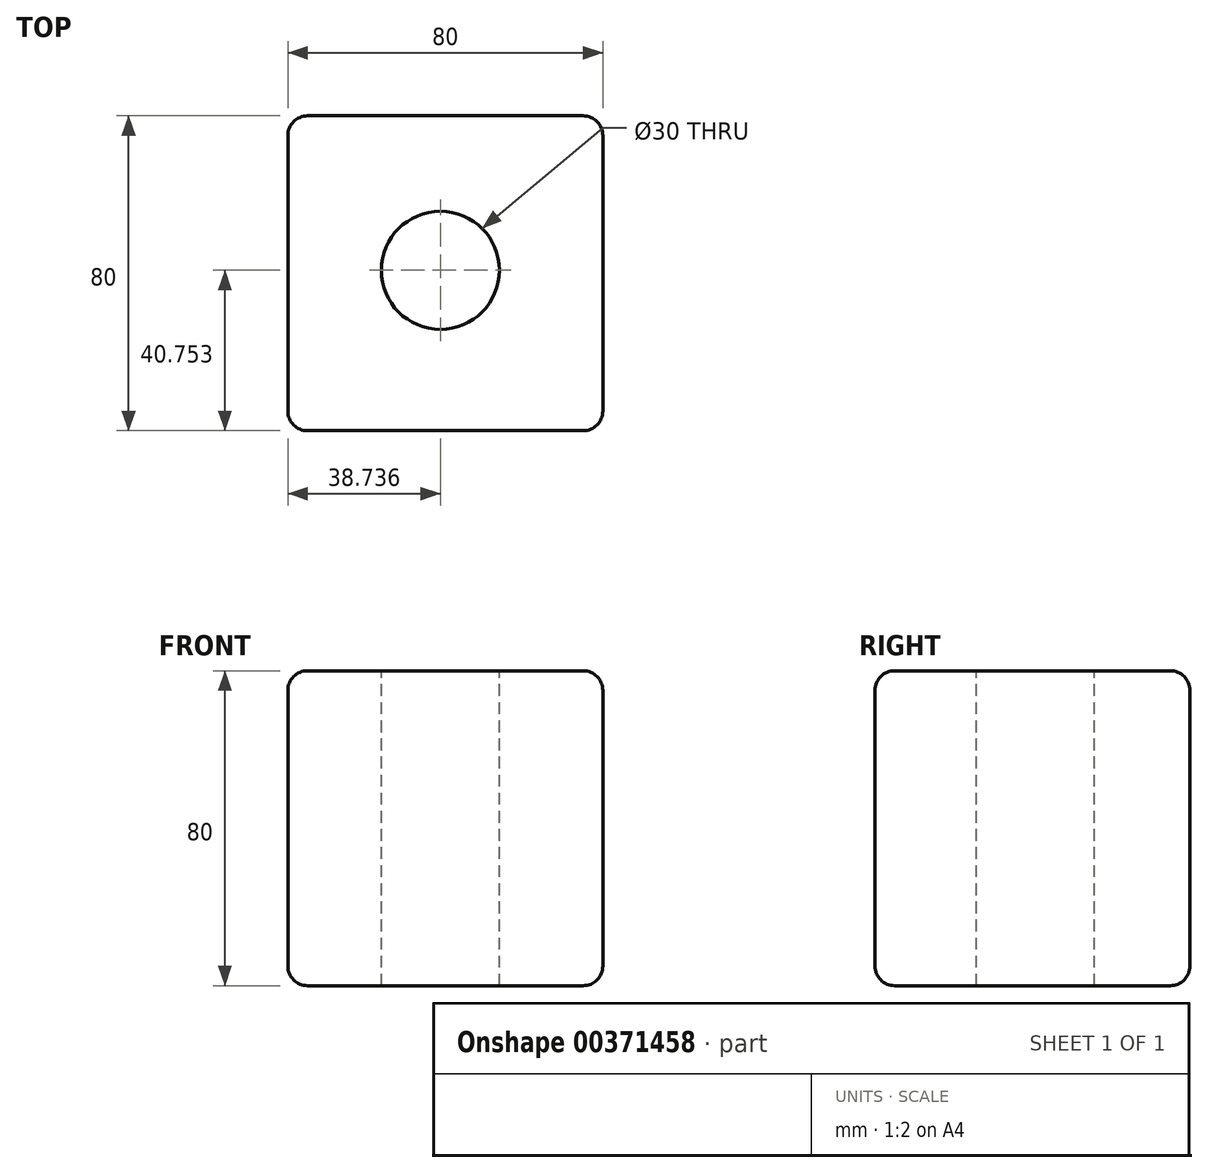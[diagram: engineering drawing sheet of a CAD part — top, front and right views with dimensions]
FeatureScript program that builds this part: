
annotation { "Feature Type Name" : "Feature", "Feature Type Description" : "" }
export const myFeature = defineFeature(function(context is Context, id is Id, definition is map)
    precondition{}
    {
        {
            var Q0;
            Q0=qCreatedBy(makeId("Top.planeOp"),FACE);
            var sketch = newSketch(context, id + "F0", { "sketchPlane" : qUnion([Q0])});
            skLineSegment(sketch, "E0.bottom", {"start": v(-77.96, 64.75) * mm, "end": v(2.04, 64.75) * mm});
            skLineSegment(sketch, "E0.top", {"start": v(-77.96, -15.25) * mm, "end": v(2.04, -15.25) * mm});
            skLineSegment(sketch, "E0.left", {"start": v(-77.96, 64.75) * mm, "end": v(-77.96, -15.25) * mm});
            skLineSegment(sketch, "E0.right", {"start": v(2.04, 64.75) * mm, "end": v(2.04, -15.25) * mm});
            skSolve(sketch);
        }
        {
            var Q0;
            Q0=makeQuery(id+"F0.imprint","IMPRINT",FACE,{"disambiguationData":[TD([[makeQuery(id+"F0.imprint","IMPRINT",EDGE,{"derivedFrom":sQuery(id+"F0.wireOp",EDGE,"E0.bottom")}),-1.0]])]});
            extrude(context, id + "F1", {"entities" : qUnion([Q0]), "depth" : 80 * mm});
        }
        {
            var Q0;
            Q0=makeQuery(id+"F1.opExtrude","CAP_FACE",FACE,{"disambiguationData":[OSD([sQuery(id+"F0.wireOp",EDGE,"E0.bottom"),sQuery(id+"F0.wireOp",EDGE,"E0.top"),sQuery(id+"F0.wireOp",EDGE,"E0.left"),sQuery(id+"F0.wireOp",EDGE,"E0.right")])],"isStart":false});
            var sketch = newSketch(context, id + "F2", { "sketchPlane" : qUnion([Q0])});
            skCircle(sketch, "E1", {"center": v(-39.22, 25.5) * mm, "radius": 15 * mm});
            skSolve(sketch);
        }
        {
            var Q0;
            Q0=makeQuery(id+"F2.imprint","IMPRINT",FACE,{"disambiguationData":[TD([[makeQuery(id+"F2.imprint","IMPRINT",EDGE,{"derivedFrom":sQuery(id+"F2.wireOp",EDGE,"E1")}),1.0]])]});
            extrude(context, id + "F3", {"entities" : qUnion([Q0]), "operationType" : NewBodyOperationType.REMOVE, "endBound" : BoundingType.THROUGH_ALL, "oppositeDirection" : true, "depth" : 25 * mm});
        }
        {
            var Q0;
            Q0=makeQuery(id+"F1.opExtrude","CAP_EDGE",EDGE,{"disambiguationData":[OSD([sQuery(id+"F0.wireOp",EDGE,"E0.bottom")])],"isStart":false});
            var Q1;
            Q1=makeQuery(id+"F1.opExtrude","CAP_EDGE",EDGE,{"disambiguationData":[OSD([sQuery(id+"F0.wireOp",EDGE,"E0.top")])],"isStart":false});
            var Q2;
            Q2=makeQuery(id+"F1.opExtrude","CAP_EDGE",EDGE,{"disambiguationData":[OSD([sQuery(id+"F0.wireOp",EDGE,"E0.left")])],"isStart":false});
            var Q3;
            Q3=makeQuery(id+"F1.opExtrude","SWEPT_EDGE",EDGE,{"disambiguationData":[OSD([sQuery(id+"F0.wireOp",EDGE,"E0.top"),sQuery(id+"F0.wireOp",EDGE,"E0.left")])]});
            var Q4;
            Q4=makeQuery(id+"F1.opExtrude","CAP_EDGE",EDGE,{"disambiguationData":[OSD([sQuery(id+"F0.wireOp",EDGE,"E0.left")])],"isStart":true});
            var Q5;
            Q5=makeQuery(id+"F1.opExtrude","SWEPT_EDGE",EDGE,{"disambiguationData":[OSD([sQuery(id+"F0.wireOp",EDGE,"E0.bottom"),sQuery(id+"F0.wireOp",EDGE,"E0.left")])]});
            var Q6;
            Q6=makeQuery(id+"F1.opExtrude","CAP_EDGE",EDGE,{"disambiguationData":[OSD([sQuery(id+"F0.wireOp",EDGE,"E0.right")])],"isStart":true});
            var Q7;
            Q7=makeQuery(id+"F1.opExtrude","SWEPT_FACE",FACE,{"disambiguationData":[OSD([sQuery(id+"F0.wireOp",EDGE,"E0.top")])]});
            var Q8;
            Q8=makeQuery(id+"F1.opExtrude","SWEPT_EDGE",EDGE,{"disambiguationData":[OSD([sQuery(id+"F0.wireOp",EDGE,"E0.top"),sQuery(id+"F0.wireOp",EDGE,"E0.right")])]});
            var Q9;
            Q9=makeQuery(id+"F1.opExtrude","CAP_EDGE",EDGE,{"disambiguationData":[OSD([sQuery(id+"F0.wireOp",EDGE,"E0.right")])],"isStart":false});
            var Q10;
            Q10=makeQuery(id+"F1.opExtrude","CAP_EDGE",EDGE,{"disambiguationData":[OSD([sQuery(id+"F0.wireOp",EDGE,"E0.bottom")])],"isStart":true});
            var Q11;
            Q11=makeQuery(id+"F1.opExtrude","SWEPT_EDGE",EDGE,{"disambiguationData":[OSD([sQuery(id+"F0.wireOp",EDGE,"E0.bottom"),sQuery(id+"F0.wireOp",EDGE,"E0.right")])]});
            fillet(context, id + "F4", {"entities" : qUnion([Q0, Q1, Q2, Q3, Q4, Q5, Q6, Q7, Q8, Q9, Q10, Q11]), "radius" : 5 * mm, "tangentPropagation" : true, "allowEdgeOverflow" : false});
        }
    });
